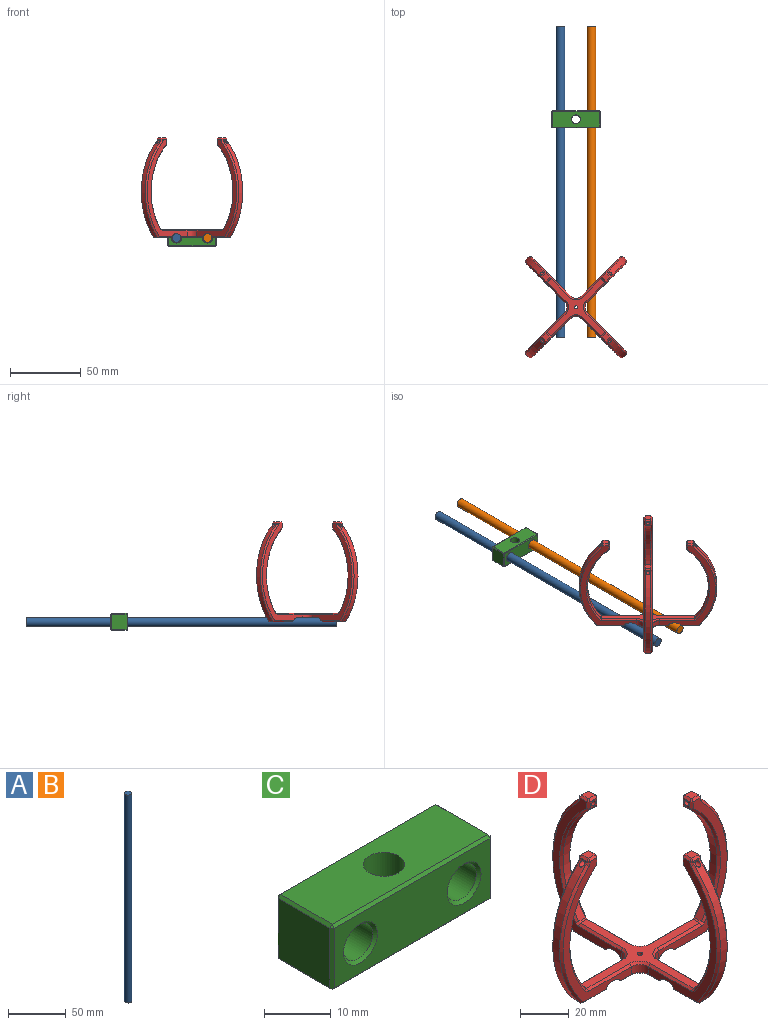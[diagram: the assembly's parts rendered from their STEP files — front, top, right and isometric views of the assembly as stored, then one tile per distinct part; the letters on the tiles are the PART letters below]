
ASSEMBLY  parts=4 mates=3
PART A: 3 faces, bbox 6.2x6.2x220 mm
  f0: cylinder r=3.1mm len=220mm, axis (0,0,-1), area 4285.1mm2, adj f1,f2
  f1: plane 6.2x6.2mm, normal (0,0,1), area 30.2mm2, adj f0
  f2: plane 6.2x6.2mm, normal (0,0,-1), area 30.2mm2, adj f0
PART B: same geometry as A
PART C: 34 faces, bbox 34x12x12 mm
  f0: plane 11x11mm, normal (-1,0,0), area 121mm2, adj f15,f24,f25,f29
  f1: plane 33x11mm, normal (0,0,-1), area 322.3mm2, adj f9,f10,f14,f15,f16
  f2: plane 11x11mm, normal (1,0,0), area 121mm2, adj f10,f13,f17,f18
  f3: cylinder r=3.1mm len=11mm, axis (0,1,0), area 214.3mm2, adj f30,f32
  f4: plane 33x11mm, normal (0,0,1), area 332.8mm2, adj f8,f18,f23,f26,f29
  f5: cylinder r=3.1mm len=11mm, axis (0,1,0), area 214.3mm2, adj f31,f33
  f6: plane 33x11mm, normal (0,-1,0), area 281.6mm2, adj f13,f14,f23,f24,f32,f33
  f7: plane 33x11mm, normal (0,1,0), area 281.6mm2, adj f16,f17,f25,f26,f30,f31
  f8: cylinder r=3.1mm len=11.5mm, axis (0,0,-1), area 224mm2, adj f4,f9
  f9: cone r=3.6mm half-angle=45deg, axis (0,0,-1), area 14.9mm2, adj f1,f8
  f10: plane 11x0.5mm, normal (0.71,0,-0.71), area 7.8mm2, adj f1,f2,f11,f12
  f11: plane 0.5x0.5mm, normal (0.58,-0.58,-0.58), area 0.2mm2, adj f10,f13,f14
  f12: plane 0.5x0.5mm, normal (0.58,0.58,-0.58), area 0.2mm2, adj f10,f16,f17
  f13: plane 11x0.5mm, normal (0.71,-0.71,0), area 7.8mm2, adj f2,f6,f11,f19
  f14: plane 33x0.5mm, normal (0,-0.71,-0.71), area 23.3mm2, adj f1,f6,f11,f20
  f15: plane 11x0.5mm, normal (-0.71,0,-0.71), area 7.8mm2, adj f0,f1,f20,f21
  f16: plane 33x0.5mm, normal (0,0.71,-0.71), area 23.3mm2, adj f1,f7,f12,f21
  f17: plane 11x0.5mm, normal (0.71,0.71,0), area 7.8mm2, adj f2,f7,f12,f22
  f18: plane 11x0.5mm, normal (0.71,0,0.71), area 7.8mm2, adj f2,f4,f19,f22
  f19: plane 0.5x0.5mm, normal (0.58,-0.58,0.58), area 0.2mm2, adj f13,f18,f23
  f20: plane 0.5x0.5mm, normal (-0.58,-0.58,-0.58), area 0.2mm2, adj f14,f15,f24
  f21: plane 0.5x0.5mm, normal (-0.58,0.58,-0.58), area 0.2mm2, adj f15,f16,f25
  f22: plane 0.5x0.5mm, normal (0.58,0.58,0.58), area 0.2mm2, adj f17,f18,f26
  f23: plane 33x0.5mm, normal (0,-0.71,0.71), area 23.3mm2, adj f4,f6,f19,f27
  f24: plane 11x0.5mm, normal (-0.71,-0.71,0), area 7.8mm2, adj f0,f6,f20,f27
  f25: plane 11x0.5mm, normal (-0.71,0.71,0), area 7.8mm2, adj f0,f7,f21,f28
  f26: plane 33x0.5mm, normal (0,0.71,0.71), area 23.3mm2, adj f4,f7,f22,f28
  f27: plane 0.5x0.5mm, normal (-0.58,-0.58,0.58), area 0.2mm2, adj f23,f24,f29
  f28: plane 0.5x0.5mm, normal (-0.58,0.58,0.58), area 0.2mm2, adj f25,f26,f29
  f29: plane 11x0.5mm, normal (-0.71,0,0.71), area 7.8mm2, adj f0,f4,f27,f28
  f30: cone r=3.6mm half-angle=45deg, axis (0,1,0), area 14.9mm2, adj f3,f7
  f31: cone r=3.6mm half-angle=45deg, axis (0,1,0), area 14.9mm2, adj f5,f7
  f32: cone r=3.1mm half-angle=45deg, axis (0,-1,0), area 14.9mm2, adj f3,f6
  f33: cone r=3.1mm half-angle=45deg, axis (0,-1,0), area 14.9mm2, adj f5,f6
PART D: 197 faces, bbox 97.6x97.6x71.1 mm
  f0: cylinder r=48.78mm len=68.08mm, axis (0,1,0), area 291.5mm2, adj f3,f137,f138,f149,f150,f192
  f1: cylinder r=48.78mm len=68.08mm, axis (0,-1,0), area 291.5mm2, adj f2,f123,f124,f140,f141,f193
  f2: plane 1.39x0.81mm, normal (0.92,0,0.4), area 0.8mm2, adj f1,f39,f133,f193
  f3: plane 1.39x0.81mm, normal (-0.92,0,0.4), area 0.8mm2, adj f0,f26,f144,f192
  f4: cylinder r=48.78mm len=68.08mm, axis (-1,0,0), area 291.5mm2, adj f6,f76,f77,f97,f98,f191
  f5: cylinder r=48.78mm len=68.08mm, axis (1,0,0), area 291.5mm2, adj f7,f169,f170,f179,f180,f190
  f6: plane 1.39x0.81mm, normal (0,-0.92,0.4), area 0.8mm2, adj f4,f33,f87,f191
  f7: plane 1.39x0.81mm, normal (0,0.92,0.4), area 0.8mm2, adj f5,f44,f183,f190
  f8: plane 26.26x26.26mm, normal (0,0,-1), area 183.8mm2, adj f15,f17,f18,f19,f99,f112,f121,f122
  f9: plane 17.65x3.91mm, normal (0,0,-1), area 61.4mm2, adj f14,f16,f140,f188
  f10: plane 17.65x3.91mm, normal (0,0,-1), area 61.4mm2, adj f160,f168,f169,f186
  f11: plane 17.65x3.91mm, normal (0,0,-1), area 61.4mm2, adj f139,f150,f159,f187
  f12: plane 19.01x1.11mm, normal (0.71,0,-0.71), area 26.9mm2, adj f27,f29,f88,f189
  f13: plane 13.73x1.04mm, normal (-0.71,0,-0.71), area 19.6mm2, adj f27,f34,f111,f189
  f14: plane 19.01x1.11mm, normal (0,-0.71,-0.71), area 26.9mm2, adj f9,f40,f132,f188
  f15: plane 6.5x1.11mm, normal (0,-0.71,-0.71), area 8.5mm2, adj f8,f20,f131,f187
  f16: plane 13.73x1.04mm, normal (0,0.71,-0.71), area 19.6mm2, adj f9,f35,f146,f188
  f17: plane 1.22x1.04mm, normal (0,0.71,-0.71), area 1.1mm2, adj f8,f21,f164,f187
  f18: plane 6.5x1.11mm, normal (0.71,0,-0.71), area 8.5mm2, adj f8,f45,f156,f186
  f19: plane 1.22x1.04mm, normal (-0.71,0,-0.71), area 1.1mm2, adj f8,f28,f164,f186
  f20: plane 68.91x39.74mm, normal (0,-1,0), area 383.3mm2, adj f15,f46,f85,f96,f105,f106,f116,f120
  f21: plane 68.91x39.74mm, normal (0,1,0), area 383.3mm2, adj f17,f47,f108,f118,f128,f135,f136,f143
  f22: plane 65.66x65.66mm, normal (0,0,1), area 525.7mm2, adj f66,f67,f73,f83,f84,f93,f104,f105
  f23: cylinder r=42.78mm len=59.29mm, axis (0,1,0), area 258.1mm2, adj f106,f107,f127,f128
  f24: plane 3.91x3.46mm, normal (1,0,0), area 9.4mm2, adj f85,f95,f107,f108,f192
  f25: plane 3.91x3.91mm, normal (0,0,1), area 15.3mm2, adj f95,f96,f118,f119
  f26: plane 3.91x0.76mm, normal (-1,0,0), area 2.8mm2, adj f3,f119,f120,f136,f137,f192
  f27: plane 17.65x3.91mm, normal (0,0,-1), area 61.4mm2, adj f12,f13,f98,f189
  f28: plane 68.91x39.74mm, normal (-1,0,0), area 383.3mm2, adj f19,f47,f154,f158,f163,f168,f174,f179
  f29: plane 68.91x39.74mm, normal (1,0,0), area 383.3mm2, adj f12,f48,f50,f54,f55,f60,f64,f66
  f30: cylinder r=42.78mm len=59.29mm, axis (-1,0,0), area 258.1mm2, adj f55,f56,f67,f68
  f31: plane 3.91x3.46mm, normal (0,1,0), area 9.4mm2, adj f50,f53,f56,f57,f191
  f32: plane 3.91x3.91mm, normal (0,0,1), area 15.3mm2, adj f53,f54,f62,f63
  f33: plane 3.91x0.76mm, normal (0,-1,0), area 2.8mm2, adj f6,f63,f64,f75,f76,f191
  f34: plane 68.91x39.74mm, normal (-1,0,0), area 383.3mm2, adj f13,f46,f57,f62,f68,f74,f75,f84
  f35: plane 68.91x39.74mm, normal (0,1,0), area 383.3mm2, adj f16,f49,f80,f102,f103,f115,f125,f126
  f36: cylinder r=42.78mm len=59.29mm, axis (0,-1,0), area 258.1mm2, adj f81,f82,f103,f104
  f37: plane 3.91x3.46mm, normal (-1,0,0), area 9.4mm2, adj f65,f79,f80,f81,f193
  f38: plane 3.91x3.91mm, normal (0,0,1), area 15.3mm2, adj f78,f79,f101,f102
  f39: plane 3.91x0.76mm, normal (1,0,0), area 2.8mm2, adj f2,f100,f101,f124,f125,f193
  f40: plane 68.91x39.74mm, normal (0,-1,0), area 383.3mm2, adj f14,f48,f65,f78,f82,f83,f92,f100
  f41: cylinder r=42.78mm len=59.29mm, axis (1,0,0), area 258.1mm2, adj f152,f153,f162,f163
  f42: plane 3.91x3.46mm, normal (0,-1,0), area 9.4mm2, adj f161,f162,f173,f174,f190
  f43: plane 3.91x3.91mm, normal (0,0,1), area 15.3mm2, adj f172,f173,f181,f182
  f44: plane 3.91x0.76mm, normal (0,1,0), area 2.8mm2, adj f7,f171,f180,f181,f185,f190
  f45: plane 68.91x39.74mm, normal (1,0,0), area 383.3mm2, adj f18,f49,f142,f147,f152,f160,f161,f170
  f46: cylinder r=5mm len=5mm, axis (0,0,1), area 30.7mm2, adj f20,f34,f93,f131
  f47: cylinder r=5mm len=5mm, axis (0,0,-1), area 30.7mm2, adj f21,f28,f148,f164
  f48: cylinder r=5mm len=5mm, axis (0,0,1), area 30.7mm2, adj f29,f40,f73,f112
  f49: cylinder r=5mm len=5mm, axis (0,0,1), area 30.7mm2, adj f35,f45,f134,f156
  f50: plane 3.46x1.04mm, normal (0.71,0.71,0), area 5.1mm2, adj f29,f31,f51,f52
  f51: plane 1.04x1.04mm, normal (0.58,0.58,0.58), area 0.9mm2, adj f50,f53,f54
  f52: plane 1.04x1.04mm, normal (0.67,0.67,-0.31), area 0.6mm2, adj f50,f55,f56
  f53: plane 3.91x1.04mm, normal (0,0.71,0.71), area 5.8mm2, adj f31,f32,f51,f58
  f54: plane 3.91x1.04mm, normal (0.71,0,0.71), area 5.8mm2, adj f29,f32,f51,f59
  f55: cone r=42.78mm half-angle=45deg, axis (1,0,0), area 98.6mm2, adj f29,f30,f52,f60
  f56: plane 3.91x0.8mm, normal (0,0.91,-0.42), area 3.5mm2, adj f30,f31,f52,f61
  f57: plane 3.46x1.04mm, normal (-0.71,0.71,0), area 5.1mm2, adj f31,f34,f58,f61
  f58: plane 1.04x1.04mm, normal (-0.58,0.58,0.58), area 0.9mm2, adj f53,f57,f62
  f59: plane 1.04x1.04mm, normal (0.58,-0.58,0.58), area 0.9mm2, adj f54,f63,f64
  f60: plane 1.64x1.44mm, normal (0.67,0.33,0.67), area 1.9mm2, adj f29,f55,f66,f67
  f61: plane 1.04x1.04mm, normal (-0.67,0.67,-0.31), area 0.6mm2, adj f56,f57,f68
  f62: plane 3.91x1.04mm, normal (-0.71,0,0.71), area 5.8mm2, adj f32,f34,f58,f69
  f63: plane 3.91x1.04mm, normal (0,-0.71,0.71), area 5.8mm2, adj f32,f33,f59,f69
  f64: plane 1.04x1.04mm, normal (0.71,-0.71,0), area 1.1mm2, adj f29,f33,f59,f70
  f65: plane 3.46x1.04mm, normal (-0.71,-0.71,0), area 5.1mm2, adj f37,f40,f71,f72
  f66: plane 24.83x1.04mm, normal (0.71,0,0.71), area 36.7mm2, adj f22,f29,f60,f73
  f67: plane 3.91x0.82mm, normal (0,0.44,0.9), area 3.6mm2, adj f22,f30,f60,f74
  f68: cone r=43.83mm half-angle=45deg, axis (-1,0,0), area 98.6mm2, adj f30,f34,f61,f74
  f69: plane 1.04x1.04mm, normal (-0.58,-0.58,0.58), area 0.9mm2, adj f62,f63,f75
  f70: plane 1.52x1.37mm, normal (0.68,-0.68,0.29), area 1.8mm2, adj f29,f64,f76,f77
  f71: plane 1.04x1.04mm, normal (-0.58,-0.58,0.58), area 0.9mm2, adj f65,f78,f79
  f72: plane 1.04x1.04mm, normal (-0.67,-0.67,-0.31), area 0.6mm2, adj f65,f81,f82
  f73: cone r=6.04mm half-angle=45deg, axis (0,0,1), area 12.8mm2, adj f22,f48,f66,f83
  f74: plane 1.64x1.44mm, normal (-0.67,0.33,0.67), area 1.9mm2, adj f34,f67,f68,f84
  f75: plane 1.04x1.04mm, normal (-0.71,-0.71,0), area 1.1mm2, adj f33,f34,f69,f87
  f76: plane 1.39x0.81mm, normal (0,-0.92,0.4), area 0.8mm2, adj f4,f33,f70,f191
  f77: cone r=47.74mm half-angle=45deg, axis (-1,0,0), area 110.2mm2, adj f4,f29,f70,f88
  f78: plane 3.91x1.04mm, normal (0,-0.71,0.71), area 5.8mm2, adj f38,f40,f71,f89
  f79: plane 3.91x1.04mm, normal (-0.71,0,0.71), area 5.8mm2, adj f37,f38,f71,f90
  f80: plane 3.46x1.04mm, normal (-0.71,0.71,0), area 5.1mm2, adj f35,f37,f90,f91
  f81: plane 3.91x0.8mm, normal (-0.91,0,-0.42), area 3.5mm2, adj f36,f37,f72,f91
  f82: cone r=43.83mm half-angle=45deg, axis (0,-1,0), area 98.6mm2, adj f36,f40,f72,f92
  f83: plane 24.83x1.04mm, normal (0,-0.71,0.71), area 36.7mm2, adj f22,f40,f73,f92
  f84: plane 24.83x1.04mm, normal (-0.71,0,0.71), area 36.7mm2, adj f22,f34,f74,f93
  f85: plane 3.46x1.04mm, normal (0.71,-0.71,0), area 5.1mm2, adj f20,f24,f86,f94
  f86: plane 1.04x1.04mm, normal (0.58,-0.58,0.58), area 0.9mm2, adj f85,f95,f96
  f87: plane 1.52x1.37mm, normal (-0.68,-0.68,0.29), area 1.8mm2, adj f6,f34,f75,f97
  f88: plane 1.04x1.04mm, normal (0.67,-0.3,-0.67), area 0.6mm2, adj f12,f77,f98
  f89: plane 1.04x1.04mm, normal (0.58,-0.58,0.58), area 0.9mm2, adj f78,f100,f101
  f90: plane 1.04x1.04mm, normal (-0.58,0.58,0.58), area 0.9mm2, adj f79,f80,f102
  f91: plane 1.04x1.04mm, normal (-0.67,0.67,-0.31), area 0.6mm2, adj f80,f81,f103
  f92: plane 1.64x1.44mm, normal (-0.33,-0.67,0.67), area 1.9mm2, adj f40,f82,f83,f104
  f93: cone r=6.04mm half-angle=45deg, axis (0,0,1), area 12.8mm2, adj f22,f46,f84,f105
  f94: plane 1.04x1.04mm, normal (0.67,-0.67,-0.31), area 0.6mm2, adj f85,f106,f107
  f95: plane 3.91x1.04mm, normal (0.71,0,0.71), area 5.8mm2, adj f24,f25,f86,f109
  f96: plane 3.91x1.04mm, normal (0,-0.71,0.71), area 5.8mm2, adj f20,f25,f86,f110
  f97: cone r=48.78mm half-angle=45deg, axis (1,0,0), area 110.2mm2, adj f4,f34,f87,f111
  f98: plane 3.91x0.78mm, normal (0,-0.41,-0.91), area 3.3mm2, adj f4,f27,f88,f111
  f99: plane 1.22x1.04mm, normal (0.71,0,-0.71), area 1.1mm2, adj f8,f29,f112,f189
  f100: plane 1.04x1.04mm, normal (0.71,-0.71,0), area 1.1mm2, adj f39,f40,f89,f113
  f101: plane 3.91x1.04mm, normal (0.71,0,0.71), area 5.8mm2, adj f38,f39,f89,f114
  f102: plane 3.91x1.04mm, normal (0,0.71,0.71), area 5.8mm2, adj f35,f38,f90,f114
  f103: cone r=42.78mm half-angle=45deg, axis (0,1,0), area 98.6mm2, adj f35,f36,f91,f115
  f104: plane 3.91x0.82mm, normal (-0.44,0,0.9), area 3.6mm2, adj f22,f36,f92,f115
  f105: plane 24.83x1.04mm, normal (0,-0.71,0.71), area 36.7mm2, adj f20,f22,f93,f116
  f106: cone r=42.78mm half-angle=45deg, axis (0,-1,0), area 98.6mm2, adj f20,f23,f94,f116
  f107: plane 3.91x0.8mm, normal (0.91,0,-0.42), area 3.5mm2, adj f23,f24,f94,f117
  f108: plane 3.46x1.04mm, normal (0.71,0.71,0), area 5.1mm2, adj f21,f24,f109,f117
  f109: plane 1.04x1.04mm, normal (0.58,0.58,0.58), area 0.9mm2, adj f95,f108,f118
  f110: plane 1.04x1.04mm, normal (-0.58,-0.58,0.58), area 0.9mm2, adj f96,f119,f120
  f111: plane 1.04x1.04mm, normal (-0.67,-0.3,-0.67), area 0.6mm2, adj f13,f97,f98
  f112: cone r=6.04mm half-angle=45deg, axis (0,0,-1), area 12.8mm2, adj f8,f48,f99,f122
  f113: plane 1.52x1.37mm, normal (0.68,-0.68,0.29), area 1.8mm2, adj f40,f100,f123,f124
  f114: plane 1.04x1.04mm, normal (0.58,0.58,0.58), area 0.9mm2, adj f101,f102,f125
  f115: plane 1.64x1.44mm, normal (-0.33,0.67,0.67), area 1.9mm2, adj f35,f103,f104,f126
  f116: plane 1.64x1.44mm, normal (0.33,-0.67,0.67), area 1.9mm2, adj f20,f105,f106,f127
  f117: plane 1.04x1.04mm, normal (0.67,0.67,-0.31), area 0.6mm2, adj f107,f108,f128
  f118: plane 3.91x1.04mm, normal (0,0.71,0.71), area 5.8mm2, adj f21,f25,f109,f129
  f119: plane 3.91x1.04mm, normal (-0.71,0,0.71), area 5.8mm2, adj f25,f26,f110,f129
  f120: plane 1.04x1.04mm, normal (-0.71,-0.71,0), area 1.1mm2, adj f20,f26,f110,f130
  f121: plane 6.5x1.11mm, normal (-0.71,0,-0.71), area 8.5mm2, adj f8,f34,f131,f189
  f122: plane 1.22x1.04mm, normal (0,-0.71,-0.71), area 1.1mm2, adj f8,f40,f112,f188
  f123: cone r=48.78mm half-angle=45deg, axis (0,1,0), area 110.2mm2, adj f1,f40,f113,f132
  f124: plane 1.39x0.81mm, normal (0.92,0,0.4), area 0.8mm2, adj f1,f39,f113,f193
  f125: plane 1.04x1.04mm, normal (0.71,0.71,0), area 1.1mm2, adj f35,f39,f114,f133
  f126: plane 24.83x1.04mm, normal (0,0.71,0.71), area 36.7mm2, adj f22,f35,f115,f134
  f127: plane 3.91x0.82mm, normal (0.44,0,0.9), area 3.6mm2, adj f22,f23,f116,f135
  f128: cone r=43.83mm half-angle=45deg, axis (0,1,0), area 98.6mm2, adj f21,f23,f117,f135
  f129: plane 1.04x1.04mm, normal (-0.58,0.58,0.58), area 0.9mm2, adj f118,f119,f136
  f130: plane 1.52x1.37mm, normal (-0.68,-0.68,0.29), area 1.8mm2, adj f20,f120,f137,f138
  f131: cone r=6.04mm half-angle=45deg, axis (0,0,-1), area 12.8mm2, adj f8,f15,f46,f121
  f132: plane 1.04x1.04mm, normal (0.3,-0.67,-0.67), area 0.6mm2, adj f14,f123,f140
  f133: plane 1.52x1.37mm, normal (0.68,0.68,0.29), area 1.8mm2, adj f2,f35,f125,f141
  f134: cone r=6.04mm half-angle=45deg, axis (0,0,1), area 12.8mm2, adj f22,f49,f126,f142
  f135: plane 1.64x1.44mm, normal (0.33,0.67,0.67), area 1.9mm2, adj f21,f127,f128,f143
  f136: plane 1.04x1.04mm, normal (-0.71,0.71,0), area 1.1mm2, adj f21,f26,f129,f144
  f137: plane 1.39x0.81mm, normal (-0.92,0,0.4), area 0.8mm2, adj f0,f26,f130,f192
  f138: cone r=47.74mm half-angle=45deg, axis (0,1,0), area 110.2mm2, adj f0,f20,f130,f145
  f139: plane 13.73x1.04mm, normal (0,-0.71,-0.71), area 19.6mm2, adj f11,f20,f145,f187
  f140: plane 3.91x0.78mm, normal (0.41,0,-0.91), area 3.3mm2, adj f1,f9,f132,f146
  f141: cone r=47.74mm half-angle=45deg, axis (0,-1,0), area 110.2mm2, adj f1,f35,f133,f146
  f142: plane 24.83x1.04mm, normal (0.71,0,0.71), area 36.7mm2, adj f22,f45,f134,f147
  f143: plane 24.83x1.04mm, normal (0,0.71,0.71), area 36.7mm2, adj f21,f22,f135,f148
  f144: plane 1.52x1.37mm, normal (-0.68,0.68,0.29), area 1.8mm2, adj f3,f21,f136,f149
  f145: plane 1.04x1.04mm, normal (-0.3,-0.67,-0.67), area 0.6mm2, adj f138,f139,f150
  f146: plane 1.04x1.04mm, normal (0.3,0.67,-0.67), area 0.6mm2, adj f16,f140,f141
  f147: plane 1.64x1.44mm, normal (0.67,-0.33,0.67), area 1.9mm2, adj f45,f142,f152,f153
  f148: cone r=6.04mm half-angle=45deg, axis (0,0,1), area 12.8mm2, adj f22,f47,f143,f154
  f149: cone r=48.78mm half-angle=45deg, axis (0,-1,0), area 110.2mm2, adj f0,f21,f144,f155
  f150: plane 3.91x0.78mm, normal (-0.41,0,-0.91), area 3.3mm2, adj f0,f11,f145,f155
  f151: plane 6.5x1.11mm, normal (0,0.71,-0.71), area 8.5mm2, adj f8,f35,f156,f188
  f152: cone r=43.83mm half-angle=45deg, axis (1,0,0), area 98.6mm2, adj f41,f45,f147,f157
  f153: plane 3.91x0.82mm, normal (0,-0.44,0.9), area 3.6mm2, adj f22,f41,f147,f158
  f154: plane 24.83x1.04mm, normal (-0.71,0,0.71), area 36.7mm2, adj f22,f28,f148,f158
  f155: plane 1.04x1.04mm, normal (-0.3,0.67,-0.67), area 0.6mm2, adj f149,f150,f159
  f156: cone r=6.04mm half-angle=45deg, axis (0,0,-1), area 12.8mm2, adj f8,f18,f49,f151
  f157: plane 1.04x1.04mm, normal (0.67,-0.67,-0.31), area 0.6mm2, adj f152,f161,f162
  f158: plane 1.64x1.44mm, normal (-0.67,-0.33,0.67), area 1.9mm2, adj f28,f153,f154,f163
  f159: plane 19.01x1.11mm, normal (0,0.71,-0.71), area 26.9mm2, adj f11,f21,f155,f187
  f160: plane 13.73x1.04mm, normal (0.71,0,-0.71), area 19.6mm2, adj f10,f45,f165,f186
  f161: plane 3.46x1.04mm, normal (0.71,-0.71,0), area 5.1mm2, adj f42,f45,f157,f166
  f162: plane 3.91x0.8mm, normal (0,-0.91,-0.42), area 3.5mm2, adj f41,f42,f157,f167
  f163: cone r=42.78mm half-angle=45deg, axis (-1,0,0), area 98.6mm2, adj f28,f41,f158,f167
  f164: cone r=6.04mm half-angle=45deg, axis (0,0,-1), area 12.8mm2, adj f8,f17,f19,f47
  f165: plane 1.04x1.04mm, normal (0.67,0.3,-0.67), area 0.6mm2, adj f160,f169,f170
  f166: plane 1.04x1.04mm, normal (0.58,-0.58,0.58), area 0.9mm2, adj f161,f172,f173
  f167: plane 1.04x1.04mm, normal (-0.67,-0.67,-0.31), area 0.6mm2, adj f162,f163,f174
  f168: plane 19.01x1.11mm, normal (-0.71,0,-0.71), area 26.9mm2, adj f10,f28,f175,f186
  f169: plane 3.91x0.78mm, normal (0,0.41,-0.91), area 3.3mm2, adj f5,f10,f165,f175
  f170: cone r=48.78mm half-angle=45deg, axis (-1,0,0), area 110.2mm2, adj f5,f45,f165,f176
  f171: plane 1.04x1.04mm, normal (0.71,0.71,0), area 1.1mm2, adj f44,f45,f176,f177
  f172: plane 3.91x1.04mm, normal (0.71,0,0.71), area 5.8mm2, adj f43,f45,f166,f177
  f173: plane 3.91x1.04mm, normal (0,-0.71,0.71), area 5.8mm2, adj f42,f43,f166,f178
  f174: plane 3.46x1.04mm, normal (-0.71,-0.71,0), area 5.1mm2, adj f28,f42,f167,f178
  f175: plane 1.04x1.04mm, normal (-0.67,0.3,-0.67), area 0.6mm2, adj f168,f169,f179
  f176: plane 1.52x1.37mm, normal (0.68,0.68,0.29), area 1.8mm2, adj f45,f170,f171,f180
  f177: plane 1.04x1.04mm, normal (0.58,0.58,0.58), area 0.9mm2, adj f171,f172,f181
  f178: plane 1.04x1.04mm, normal (-0.58,-0.58,0.58), area 0.9mm2, adj f173,f174,f182
  f179: cone r=47.74mm half-angle=45deg, axis (1,0,0), area 110.2mm2, adj f5,f28,f175,f183
  f180: plane 1.39x0.81mm, normal (0,0.92,0.4), area 0.8mm2, adj f5,f44,f176,f190
  f181: plane 3.91x1.04mm, normal (0,0.71,0.71), area 5.8mm2, adj f43,f44,f177,f184
  f182: plane 3.91x1.04mm, normal (-0.71,0,0.71), area 5.8mm2, adj f28,f43,f178,f184
  f183: plane 1.52x1.37mm, normal (-0.68,0.68,0.29), area 1.8mm2, adj f7,f28,f179,f185
  f184: plane 1.04x1.04mm, normal (-0.58,0.58,0.58), area 0.9mm2, adj f181,f182,f185
  f185: plane 1.04x1.04mm, normal (-0.71,0.71,0), area 1.1mm2, adj f28,f44,f183,f184
  f186: cylinder r=3.1mm len=14.51mm, axis (0.71,0.71,0), area 79.6mm2, adj f8,f10,f18,f19,f28,f45,f160,f168
  f187: cylinder r=3.1mm len=14.51mm, axis (0.71,0.71,0), area 79.6mm2, adj f8,f11,f15,f17,f20,f21,f139,f159
  f188: cylinder r=3.1mm len=14.51mm, axis (0.71,0.71,0), area 79.6mm2, adj f8,f9,f14,f16,f35,f40,f122,f151
  f189: cylinder r=3.1mm len=14.51mm, axis (0.71,0.71,0), area 79.6mm2, adj f8,f12,f13,f27,f29,f34,f99,f121
  f190: cylinder r=1.15mm len=7.73mm, axis (0,1,0), area 48.6mm2, adj f5,f7,f42,f44,f180
  f191: cylinder r=1.15mm len=7.73mm, axis (0,1,0), area 48.6mm2, adj f4,f6,f31,f33,f76
  f192: cylinder r=1.15mm len=7.73mm, axis (1,0,0), area 48.6mm2, adj f0,f3,f24,f26,f137
  f193: cylinder r=1.15mm len=7.73mm, axis (1,0,0), area 48.6mm2, adj f1,f2,f37,f39,f124
  f194: cylinder r=1.15mm len=5.5mm, axis (0,0,-1), area 39.7mm2, adj f22,f196
  f195: cylinder r=1.5mm len=3mm, axis (0,0,-1), area 4.7mm2, adj f8,f196
  f196: plane 3x3mm, normal (0,0,-1), area 2.9mm2, adj f194,f195
PLACE A rot(axis=(-1,0,0),90deg) t=(50.91,-120.66,228.44)mm
PLACE B rot(axis=(-1,0,0),90deg) t=(72.91,-120.66,228.44)mm
PLACE C t=(47.14,39.34,222.44)mm
PLACE D rot(axis=(0,0,-1),135deg) t=(136.38,-10.42,228.44)mm
MATE fastened B.f0 <-> D.f186  axis (0,-1,0) through (58.14,-120.66,228.44)mm
MATE fastened A.f0 <-> D.f188  axis (0,-1,0) through (36.14,-120.66,228.44)mm
MATE fastened A.f0 <-> C.f3  axis (0,1,0) through (36.14,99.34,228.44)mm
